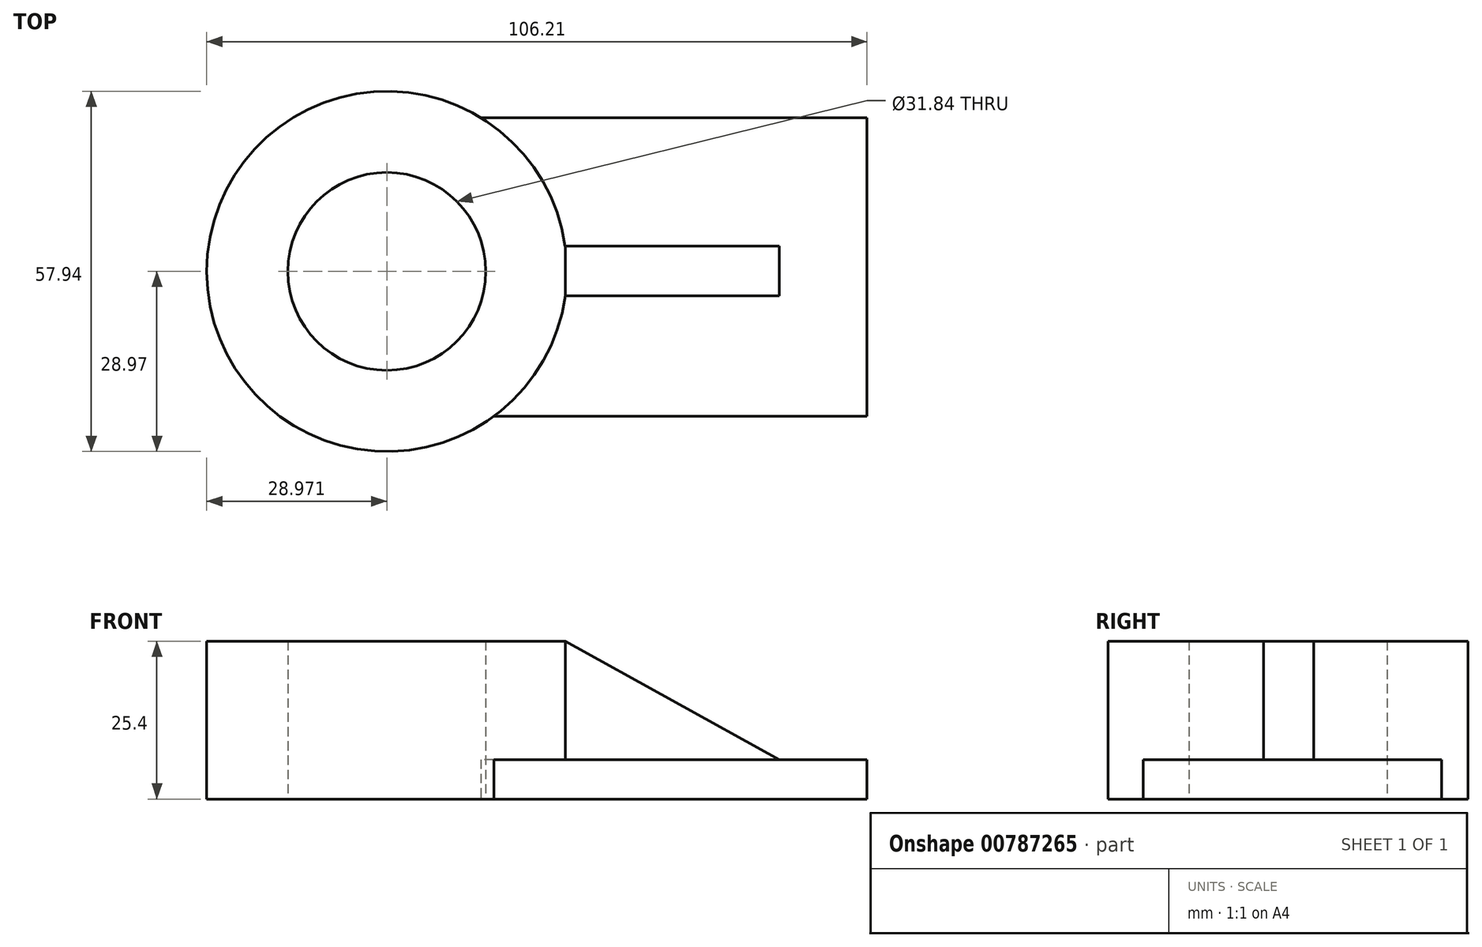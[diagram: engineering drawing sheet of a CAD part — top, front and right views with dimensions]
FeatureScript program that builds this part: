
annotation { "Feature Type Name" : "Feature", "Feature Type Description" : "" }
export const myFeature = defineFeature(function(context is Context, id is Id, definition is map)
    precondition{}
    {
        {
            var Q0;
            Q0=qCreatedBy(makeId("Top.planeOp"),FACE);
            var sketch = newSketch(context, id + "F0", { "sketchPlane" : qUnion([Q0])});
            skCircle(sketch, "E0", {"center": v(-46.58, 0) * mm, "radius": 15.92 * mm});
            skArc(sketch, "E1", {"start": v(-46.3, 28.97) * mm, "mid": v(-75.55, 0) * mm, "end": v(-46.3, -28.97) * mm});
            skArc(sketch, "E2", {"start": v(-46.3, -28.97) * mm, "mid": v(-17.6, 0) * mm, "end": v(-46.3, 28.97) * mm});
            skLineSegment(sketch, "E3", {"start": v(30.66, 0) * mm, "end": v(30.66, 24.7) * mm});
            skLineSegment(sketch, "E4", {"start": v(30.66, 0) * mm, "end": v(30.66, -23.3) * mm});
            skPoint(sketch, "E5.center.orphan", {"position": v(46.58, 0) * mm});
            skLineSegment(sketch, "E6", {"start": v(30.66, 24.7) * mm, "end": v(-31.42, 24.7) * mm});
            skLineSegment(sketch, "E7", {"start": v(30.66, -23.3) * mm, "end": v(-29.34, -23.3) * mm});
            skSolve(sketch);
        }
        {
            var Q0;
            Q0=makeQuery(id+"F0.imprint","IMPRINT",FACE,{"disambiguationData":[TD([[makeQuery(id+"F0.imprint","IMPRINT",EDGE,{"derivedFrom":sQuery(id+"F0.wireOp",EDGE,"E0")}),-1.0]])]});
            extrude(context, id + "F1", {"entities" : qUnion([Q0]), "depth" : 25.4 * mm, "offsetDistance" : 25.4 * mm});
        }
        {
            var Q0;
            Q0=makeQuery(id+"F0.imprint","IMPRINT",FACE,{"disambiguationData":[TD([[makeQuery(id+"F0.imprint","IMPRINT",EDGE,{"derivedFrom":sQuery(id+"F0.wireOp",EDGE,"E3")}),1.0]])]});
            extrude(context, id + "F2", {"entities" : qUnion([Q0]), "operationType" : NewBodyOperationType.ADD, "depth" : 6.35 * mm, "offsetDistance" : 25.4 * mm});
        }
        {
            var Q0;
            Q0=makeQuery(id+"F2.opExtrude","CAP_FACE",FACE,{"disambiguationData":[OSD([sQuery(id+"F0.wireOp",EDGE,"E2"),sQuery(id+"F0.wireOp",EDGE,"E3"),sQuery(id+"F0.wireOp",EDGE,"E4"),sQuery(id+"F0.wireOp",EDGE,"E6"),sQuery(id+"F0.wireOp",EDGE,"E7")])],"isStart":false});
            var sketch = newSketch(context, id + "F3", { "sketchPlane" : qUnion([Q0])});
            skLineSegment(sketch, "E8.bottom", {"start": v(-17.9, 4.1) * mm, "end": v(16.55, 4.1) * mm});
            skLineSegment(sketch, "E8.top", {"start": v(-17.9, -3.96) * mm, "end": v(16.55, -3.96) * mm});
            skLineSegment(sketch, "E8.left", {"start": v(-17.9, 4.1) * mm, "end": v(-17.9, -3.96) * mm});
            skLineSegment(sketch, "E8.right", {"start": v(16.55, 4.1) * mm, "end": v(16.55, -3.96) * mm});
            skSolve(sketch);
        }
        {
            var Q0;
            {var subQ0=sQuery(id+"F3.wireOp",EDGE,"E8.bottom");Q0=makeQuery(id+"F3.imprint","IMPRINT",FACE,{"disambiguationData":[TD([[makeQuery(id+"F3.imprint","IMPRINT",EDGE,{"derivedFrom":subQ0}),-1.0]])]});}
            extrude(context, id + "F4", {"entities" : qUnion([Q0]), "operationType" : NewBodyOperationType.ADD, "depth" : 19.05 * mm, "offsetDistance" : 25.4 * mm});
        }
        {
            var Q0;
            Q0=makeQuery(id+"F4.opExtrude","SWEPT_FACE",FACE,{"disambiguationData":[OSD([sQuery(id+"F3.wireOp",EDGE,"E8.top")])]});
            var sketch = newSketch(context, id + "F5", { "sketchPlane" : qUnion([Q0])});
            skLineSegment(sketch, "E9", {"start": v(-17.88, 25.4) * mm, "end": v(16.55, 6.35) * mm});
            skSolve(sketch);
        }
        {
            var Q0;
            Q0=makeQuery(id+"F5.imprint","IMPRINT",FACE,{"disambiguationData":[TD([[makeQuery(id+"F5.imprint","IMPRINT",EDGE,{"derivedFrom":sQuery(id+"F5.wireOp",EDGE,"E9")}),1.0]])]});
            extrude(context, id + "F6", {"entities" : qUnion([Q0]), "operationType" : NewBodyOperationType.REMOVE, "oppositeDirection" : true, "depth" : 1752.6 * mm, "offsetDistance" : 25.4 * mm});
        }
    });
